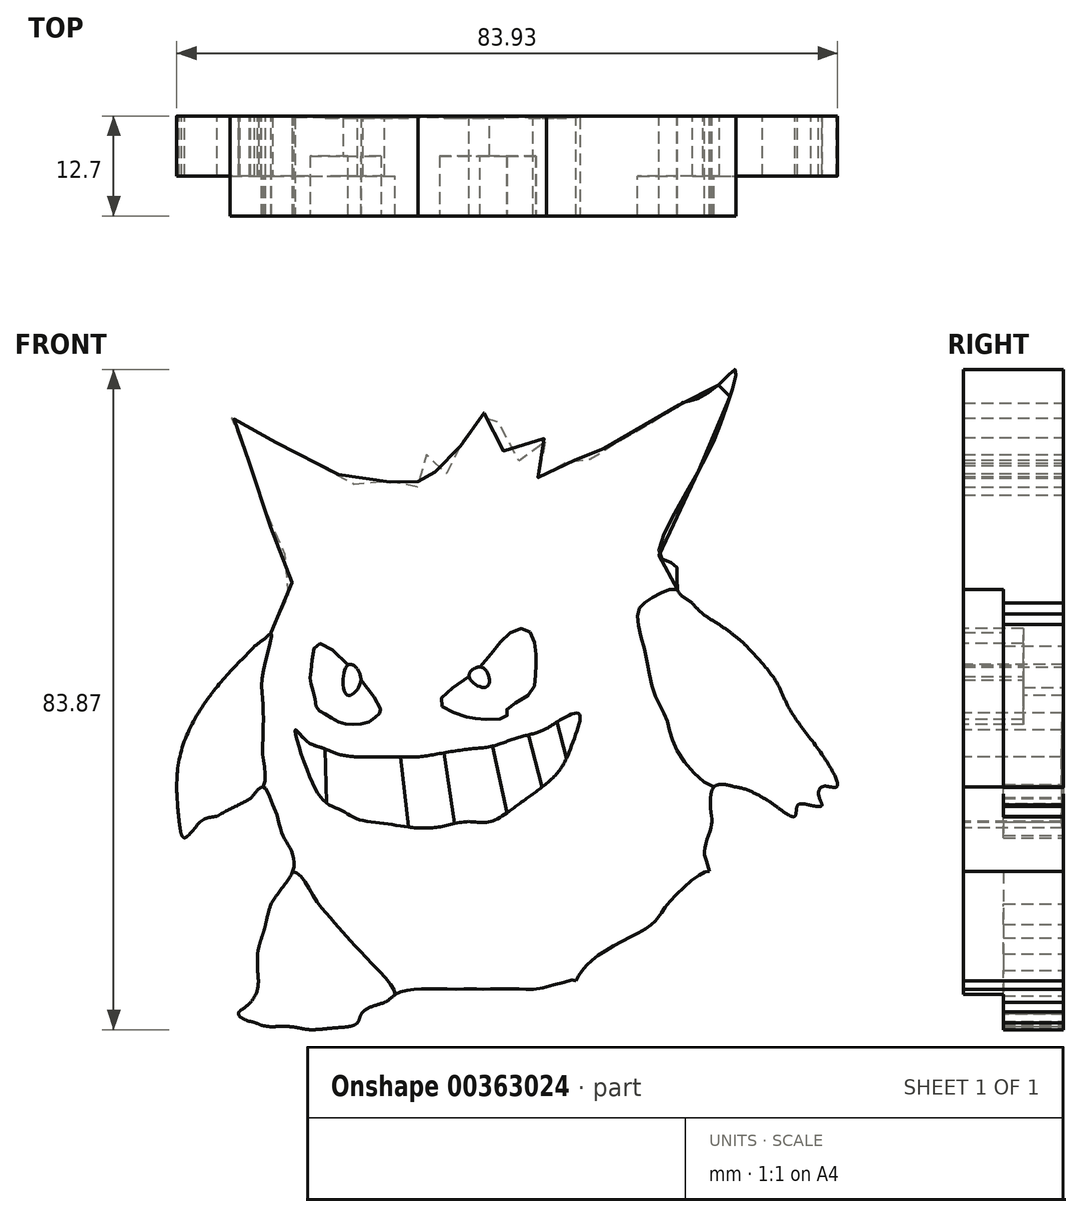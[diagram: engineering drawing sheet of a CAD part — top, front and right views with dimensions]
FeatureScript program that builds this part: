
annotation { "Feature Type Name" : "Feature", "Feature Type Description" : "" }
export const myFeature = defineFeature(function(context is Context, id is Id, definition is map)
    precondition{}
    {
        {
            var Q0;
            Q0=qCreatedBy(makeId("Front.planeOp"),FACE);
            var sketch = newSketch(context, id + "F0", { "sketchPlane" : qUnion([Q0])});
            skPoint(sketch, "E0.93.internal.snap0", {"position": v(-42.85, 9.92) * mm});
            skFitSpline(sketch, "E0", {"points": [v(-15.9, 37.28) * mm, v(-21.04, 39.5) * mm, v(-27.22, 42.6) * mm, v(-32.02, 45.34) * mm, v(-34.08, 46.36) * mm, v(-35.1, 46.88) * mm, v(-33.4, 42.93) * mm, v(-31.85, 38.48) * mm, v(-29.1, 31.1) * mm, v(-27.22, 27.16) * mm, v(-28.6, 22.35) * mm, v(-29.96, 19.61) * mm, v(-32.02, 17.9) * mm, v(-37.5, 11.9) * mm, v(-41.62, 3.49) * mm, v(-41.62, -4.4) * mm, v(-40.94, -6.46) * mm, v(-38.88, -4.4) * mm, v(-36.82, -3.71) * mm, v(-33.4, -2.34) * mm, v(-31, 0) * mm, v(-29.96, -1.66) * mm, v(-29.28, -3.37) * mm, v(-28.6, -5.77) * mm, v(-27.9, -7.14) * mm, v(-27.22, -8.52) * mm, v(-27.22, -10.75) * mm, v(-29.96, -14.86) * mm, v(-30.65, -17.43) * mm, v(-31.16, -19.15) * mm, v(-31.68, -21.2) * mm, v(-31.68, -23.27) * mm, v(-32.02, -25.15) * mm, v(-32.02, -25.67) * mm, v(-32.02, -26.52) * mm, v(-33.4, -28.07) * mm, v(-34.08, -28.75) * mm, v(-33.4, -29.95) * mm, v(-32.7, -29.78) * mm, v(-30.65, -30.47) * mm, v(-29.8, -30.47) * mm, v(-27.22, -30.47) * mm, v(-25.16, -30.81) * mm, v(-22.42, -30.64) * mm, v(-20.36, -30.47) * mm, v(-18.99, -29.95) * mm, v(-18.3, -28.58) * mm, v(-15.56, -27.38) * mm, v(-14.18, -26.35) * mm, v(-12.81, -25.84) * mm, v(-10.75, -25.67) * mm, v(-8, -25.67) * mm, v(-5.27, -25.67) * mm, v(-3.9, -25.67) * mm, v(-1.84, -25.67) * mm, v(1.6, -25.67) * mm, v(3.65, -25.67) * mm, v(7.77, -24.64) * mm, v(8.8, -24.64) * mm, v(8.8, -26.7) * mm, v(9.83, -27.9) * mm, v(10.86, -29.78) * mm, v(12.91, -30.81) * mm, v(13.26, -33.2) * mm, v(15.32, -31.5) * mm, v(18.06, -33.2) * mm, v(20.29, -33.2) * mm, v(20.8, -31.5) * mm, v(22.86, -31.5) * mm, v(24.92, -31.5) * mm, v(24.92, -29.78) * mm, v(23.55, -27.72) * mm, v(24.92, -22.92) * mm, v(24.92, -20.35) * mm, v(24.92, -17.78) * mm, v(24.92, -15.55) * mm, v(25.6, -13.66) * mm, v(25.6, -10.23) * mm, v(25.1, -8.17) * mm, v(25.95, -5.09) * mm, v(25.95, -3.37) * mm, v(26.3, 0) * mm, v(29.04, 0) * mm, v(32.47, -1.31) * mm, v(34.52, -2.69) * mm, v(36.58, -3.71) * mm, v(36.92, -2.34) * mm, v(38.64, -2.34) * mm, v(40.01, -2.34) * mm, v(39.67, -1.31) * mm, v(40.01, 0) * mm, v(41.87, 0) * mm, v(40.01, 4.17) * mm, v(35.9, 9.92) * mm, v(34.18, 13.44) * mm, v(31.1, 17.2) * mm, v(29.72, 18.58) * mm, v(26.98, 20.64) * mm, v(24.92, 22.01) * mm, v(23.55, 23.38) * mm, v(21.66, 25.1) * mm, v(21.49, 28.19) * mm, v(19.43, 29.21) * mm, v(23.9, 39.33) * mm, v(27.66, 47.57) * mm, v(29.04, 53.03) * mm, v(26.98, 51.17) * mm, v(23.55, 49.1) * mm, v(22.18, 48.77) * mm, v(20.8, 47.4) * mm, v(18.92, 46.36) * mm, v(16, 45.34) * mm, v(13.26, 43.28) * mm, v(11.37, 42.6) * mm, v(9.83, 40.88) * mm, v(8.63, 41.56) * mm, v(5.88, 40.02) * mm, v(4.68, 39.5) * mm, v(3.3, 39.5) * mm, v(5.02, 44.3) * mm, v(2.62, 42.25) * mm, v(0, 41.56) * mm, v(-1.66, 48.77) * mm, v(-3.2, 47.05) * mm, v(-4.24, 45.68) * mm, v(-5.78, 43.62) * mm, v(-6.64, 41.22) * mm, v(-8.7, 39.5) * mm, v(-10.07, 42.25) * mm, v(-11.27, 39.5) * mm, v(-11.44, 38.13) * mm, v(-13.84, 39.85) * mm, v(-15.9, 37.28) * mm]});
            skFitSpline(sketch, "E1", {"points": [v(-26.87, 7.26) * mm, v(-25.16, 1.6) * mm, v(-22.93, -2) * mm, v(-20.87, -3.03) * mm, v(-18.99, -4.06) * mm, v(-15.9, -4.57) * mm, v(-12.47, -5.09) * mm, v(-8.7, -5.09) * mm, v(-5.1, -4.4) * mm, v(-2.18, -4.4) * mm, v(1.77, -2) * mm, v(6.4, 1.77) * mm, v(8.45, 5.89) * mm, v(9.14, 9.32) * mm, v(6.4, 8.3) * mm, v(4.34, 7.1) * mm, v(1.25, 6.23) * mm, v(-1.84, 5.2) * mm, v(-4.4, 4.86) * mm, v(-8, 4.35) * mm, v(-11.27, 3.83) * mm, v(-13.5, 3.83) * mm, v(-17.27, 3.83) * mm, v(-18.99, 3.83) * mm, v(-21.39, 4.17) * mm, v(-23.1, 4.86) * mm, v(-25.5, 5.89) * mm, v(-26.87, 7.26) * mm]});
            skFitSpline(sketch, "E2", {"points": [v(-23.79, 18.24) * mm, v(-24.82, 15.15) * mm, v(-24.99, 13.44) * mm, v(-24.47, 11.72) * mm, v(-24.13, 10) * mm, v(-23.1, 9.32) * mm, v(-21.39, 8.3) * mm, v(-19.67, 7.95) * mm, v(-17.44, 8.3) * mm, v(-16.24, 9.32) * mm, v(-16.07, 10) * mm, v(-23.79, 18.24) * mm]});
            skFitSpline(sketch, "E3", {"points": [v(-8.52, 10.7) * mm, v(-5.27, 8.98) * mm, v(-3.2, 8.63) * mm, v(0, 8.98) * mm, v(0, 9.83) * mm, v(2.97, 11.9) * mm, v(3.65, 14.64) * mm, v(3.65, 17.2) * mm, v(2.62, 19.95) * mm, v(0, 19.27) * mm, v(-3.9, 14.8) * mm, v(-8.52, 10.7) * mm]});
            skFitSpline(sketch, "E4", {"points": [v(-20.17, 15.5) * mm, v(-20.36, 11.72) * mm, v(-18.55, 13.63) * mm, v(-20.17, 15.5) * mm]});
            skFitSpline(sketch, "E5", {"points": [v(-3.04, 15.15) * mm, v(-2.52, 12.75) * mm, v(-4.8, 14.08) * mm, v(-3.04, 15.15) * mm]});
            skFitSpline(sketch, "E6", {"points": [v(-29.96, 19.61) * mm, v(-31, 14.47) * mm, v(-31, 10.35) * mm, v(-31, 6.23) * mm, v(-31, 3.83) * mm, v(-31, 0) * mm, v(-36.82, -3.71) * mm, v(-40.94, -6.46) * mm, v(-41.62, -4.4) * mm, v(-41.62, 3.49) * mm, v(-37.5, 11.9) * mm, v(-32.02, 17.9) * mm, v(-29.96, 19.61) * mm]});
            skFitSpline(sketch, "E7", {"points": [v(26.3, 0) * mm, v(21.49, 4.86) * mm, v(20.29, 8.63) * mm, v(18.75, 11.9) * mm, v(17.37, 17.9) * mm, v(16.69, 22.35) * mm, v(18.75, 24.24) * mm, v(21.66, 25.1) * mm, v(23.55, 23.38) * mm, v(24.92, 22.01) * mm, v(26.98, 20.64) * mm, v(29.72, 18.58) * mm, v(31.1, 17.2) * mm, v(34.18, 13.44) * mm, v(35.9, 9.92) * mm, v(40.01, 4.17) * mm, v(41.87, 0) * mm, v(40.01, 0) * mm, v(40.01, -2.34) * mm, v(38.64, -2.34) * mm, v(36.92, -2.34) * mm, v(36.58, -3.71) * mm, v(34.52, -2.69) * mm, v(32.47, -1.31) * mm, v(29.04, 0) * mm, v(26.3, 0) * mm]});
            skFitSpline(sketch, "E8", {"points": [v(-27.22, -10.75) * mm, v(-24.47, -14) * mm, v(-21.39, -17.78) * mm, v(-18.3, -21.2) * mm, v(-14.18, -26.35) * mm, v(-15.56, -27.38) * mm, v(-18.3, -28.58) * mm, v(-18.99, -29.95) * mm, v(-20.36, -30.47) * mm, v(-22.42, -30.64) * mm, v(-25.16, -30.81) * mm, v(-27.22, -30.47) * mm, v(-29.8, -30.47) * mm, v(-32.7, -29.78) * mm, v(-34.08, -28.75) * mm, v(-32.02, -26.52) * mm, v(-31.68, -23.27) * mm, v(-31.68, -21.2) * mm, v(-31.16, -19.15) * mm, v(-30.65, -17.43) * mm, v(-29.96, -14.86) * mm, v(-27.22, -10.75) * mm]});
            skFitSpline(sketch, "E9", {"points": [v(8.8, -24.64) * mm, v(11.88, -21.2) * mm, v(18.4, -17.43) * mm, v(20.46, -14.86) * mm, v(25.7, -10.75) * mm, v(25.6, -13.66) * mm, v(24.92, -15.55) * mm, v(24.92, -17.78) * mm, v(24.92, -20.35) * mm, v(24.92, -22.92) * mm, v(23.55, -27.72) * mm, v(24.92, -29.78) * mm, v(24.92, -31.5) * mm, v(22.86, -31.5) * mm, v(20.8, -31.5) * mm, v(20.29, -33.2) * mm, v(18.06, -33.2) * mm, v(15.32, -31.5) * mm, v(13.26, -33.2) * mm, v(12.91, -30.81) * mm, v(10.86, -29.78) * mm, v(9.83, -27.9) * mm, v(8.8, -26.7) * mm, v(8.8, -24.64) * mm]});
            skLineSegment(sketch, "E10", {"start": v(-23.1, 4.86) * mm, "end": v(-22.93, -2) * mm});
            skLineSegment(sketch, "E11", {"start": v(-18.99, 3.83) * mm, "end": v(-17.27, -4.06) * mm});
            skLineSegment(sketch, "E12", {"start": v(-13.5, 3.83) * mm, "end": v(-12.47, -5.09) * mm});
            skLineSegment(sketch, "E13", {"start": v(-8, 4.35) * mm, "end": v(-6.65, -4.64) * mm});
            skLineSegment(sketch, "E14", {"start": v(-1.84, 5.2) * mm, "end": v(0, -3.3) * mm});
            skLineSegment(sketch, "E15", {"start": v(2.76, 6.63) * mm, "end": v(4.49, 0) * mm});
            skLineSegment(sketch, "E16", {"start": v(6.4, 8.3) * mm, "end": v(7.56, 3.64) * mm});
            skSolve(sketch);
        }
        {
            var Q0;
            Q0=makeQuery(id+"F0.imprint","IMPRINT",FACE,{"disambiguationData":[TD([[makeQuery(id+"F0.imprint","IMPRINT",EDGE,{"derivedFrom":sQuery(id+"F0.wireOp",EDGE,"E1")}),-1.0]])]});
            extrude(context, id + "F1", {"entities" : qUnion([Q0]), "depth" : 12.7 * mm});
        }
        {
            var Q0;
            {var subQ0=sQuery(id+"F0.wireOp",EDGE,"E7");var subQ1=sQuery(id+"F0.wireOp",EDGE,"E0");var subQ6=makeQuery(id+"F0.imprint","INTERSECT",VERTEX,{"disambiguationData":[OD(0.0)],"derivedFrom":[subQ1,subQ0]});Q0=makeQuery(id+"F0.imprint","IMPRINT",FACE,{"disambiguationData":[TD([[makeQuery(id+"F0.imprint","IMPRINT",EDGE,{"disambiguationData":[TD([[subQ6,-1.0]])],"derivedFrom":subQ1}),1.0]])]});}
            var Q1;
            {var subQ0=sQuery(id+"F0.wireOp",EDGE,"E6");var subQ1=sQuery(id+"F0.wireOp",EDGE,"E0");var subQ11=makeQuery(id+"F0.imprint","INTERSECT",VERTEX,{"disambiguationData":[OD(0.0)],"derivedFrom":[subQ1,subQ0]});Q1=makeQuery(id+"F0.imprint","IMPRINT",FACE,{"disambiguationData":[TD([[makeQuery(id+"F0.imprint","IMPRINT",EDGE,{"disambiguationData":[TD([[subQ11,1.0]])],"derivedFrom":subQ1}),1.0]])]});}
            var Q2;
            {var subQ0=sQuery(id+"F0.wireOp",EDGE,"E8");var subQ1=sQuery(id+"F0.wireOp",EDGE,"E0");var subQ16=makeQuery(id+"F0.imprint","INTERSECT",VERTEX,{"disambiguationData":[OD(2.0)],"derivedFrom":[subQ1,subQ0]});Q2=makeQuery(id+"F0.imprint","IMPRINT",FACE,{"disambiguationData":[TD([[makeQuery(id+"F0.imprint","IMPRINT",EDGE,{"disambiguationData":[TD([[subQ16,-1.0]])],"derivedFrom":subQ1}),1.0]])]});}
            var Q3;
            {var subQ0=sQuery(id+"F0.wireOp",EDGE,"E9");var subQ1=sQuery(id+"F0.wireOp",EDGE,"E0");var subQ4=makeQuery(id+"F0.imprint","INTERSECT",VERTEX,{"disambiguationData":[OD(0.0)],"derivedFrom":[subQ1,subQ0]});var subQ6=makeQuery(id+"F0.imprint","IMPRINT",VERTEX,{"derivedFrom":subQ0});Q3=makeQuery(id+"F0.imprint","IMPRINT",FACE,{"disambiguationData":[TD([[makeQuery(id+"F0.imprint","IMPRINT",EDGE,{"disambiguationData":[TD([[subQ6,-1.0],[subQ4,1.0]])],"derivedFrom":subQ0}),-1.0]])]});}
            extrude(context, id + "F2", {"entities" : qUnion([Q0, Q1, Q2, Q3]), "operationType" : NewBodyOperationType.ADD, "depth" : 7.62 * mm});
        }
        {
            var Q0;
            {var subQ0=sQuery(id+"F0.wireOp",EDGE,"E4");var subQ1=sQuery(id+"F0.wireOp",EDGE,"E2");var subQ2=makeQuery(id+"F0.imprint","INTERSECT",VERTEX,{"disambiguationData":[OD(0.0)],"derivedFrom":[subQ1,subQ0]});Q0=makeQuery(id+"F0.imprint","IMPRINT",FACE,{"disambiguationData":[TD([[makeQuery(id+"F0.imprint","IMPRINT",EDGE,{"disambiguationData":[TD([[subQ2,-1.0]])],"derivedFrom":subQ1}),1.0]])]});}
            var Q1;
            {var subQ0=sQuery(id+"F0.wireOp",EDGE,"E5");var subQ1=sQuery(id+"F0.wireOp",EDGE,"E3");var subQ2=makeQuery(id+"F0.imprint","INTERSECT",VERTEX,{"disambiguationData":[OD(0.0)],"derivedFrom":[subQ1,subQ0]});Q1=makeQuery(id+"F0.imprint","IMPRINT",FACE,{"disambiguationData":[TD([[makeQuery(id+"F0.imprint","IMPRINT",EDGE,{"disambiguationData":[TD([[subQ2,-1.0]])],"derivedFrom":subQ1}),1.0]])]});}
            extrude(context, id + "F3", {"entities" : qUnion([Q0, Q1]), "operationType" : NewBodyOperationType.ADD, "depth" : 5.08 * mm});
        }
        {
            var Q0;
            Q0=sQuery(id+"F0.wireOp",EDGE,"E4");
            extrude(context, id + "F4", {"bodyType" : ToolBodyType.SURFACE, "surfaceEntities" : qUnion([Q0]), "depth" : 5.08 * mm});
        }
        {
            var Q0;
            Q0=sQuery(id+"F0.wireOp",EDGE,"E4");
            var Q1;
            Q1=sQuery(id+"F0.wireOp",EDGE,"E5");
            extrude(context, id + "F5", {"bodyType" : ToolBodyType.SURFACE, "surfaceEntities" : qUnion([Q0, Q1]), "depth" : 12.7 * mm});
        }
        {
            var Q0;
            {var subQ0=sQuery(id+"F0.wireOp",EDGE,"E6");var subQ1=sQuery(id+"F0.wireOp",EDGE,"E0");Q0=makeQuery(id+"F2.opExtrude","SWEPT_EDGE",EDGE,{"disambiguationData":[OSD([subQ1,subQ0]),TDD([makeQuery(id+"F0.imprint","INTERSECT",VERTEX,{"disambiguationData":[OD(2.0)],"derivedFrom":[subQ1,subQ0]})])]});}
            fillet(context, id + "F6", {"entities" : qUnion([Q0]), "radius" : 5.08 * mm, "tangentPropagation" : true, "allowEdgeOverflow" : false});
        }
        {
            var Q0;
            {var subQ0=sQuery(id+"F0.wireOp",EDGE,"E10");Q0=makeQuery(id+"F0.imprint","IMPRINT",FACE,{"disambiguationData":[TD([[makeQuery(id+"F0.imprint","IMPRINT",EDGE,{"derivedFrom":subQ0}),-1.0]])]});}
            extrude(context, id + "F7", {"entities" : qUnion([Q0]), "operationType" : NewBodyOperationType.ADD, "depth" : 0.15 * mm});
        }
        {
            var Q0;
            {var subQ0=sQuery(id+"F0.wireOp",EDGE,"E10");Q0=makeQuery(id+"F0.imprint","IMPRINT",FACE,{"disambiguationData":[TD([[makeQuery(id+"F0.imprint","IMPRINT",EDGE,{"derivedFrom":subQ0}),1.0]])]});}
            var Q1;
            {var subQ0=sQuery(id+"F0.wireOp",EDGE,"E13");Q1=makeQuery(id+"F0.imprint","IMPRINT",FACE,{"disambiguationData":[TD([[makeQuery(id+"F0.imprint","IMPRINT",EDGE,{"derivedFrom":subQ0}),1.0]])]});}
            var Q2;
            {var subQ0=sQuery(id+"F0.wireOp",EDGE,"E15");Q2=makeQuery(id+"F0.imprint","IMPRINT",FACE,{"disambiguationData":[TD([[makeQuery(id+"F0.imprint","IMPRINT",EDGE,{"derivedFrom":subQ0}),1.0]])]});}
            extrude(context, id + "F8", {"entities" : qUnion([Q0, Q1, Q2]), "operationType" : NewBodyOperationType.ADD, "depth" : 0.25 * mm});
        }
        {
            var Q0;
            {var subQ0=sQuery(id+"F0.wireOp",EDGE,"E12");Q0=makeQuery(id+"F0.imprint","IMPRINT",FACE,{"disambiguationData":[TD([[makeQuery(id+"F0.imprint","IMPRINT",EDGE,{"derivedFrom":subQ0}),1.0]])]});}
            var Q1;
            {var subQ0=sQuery(id+"F0.wireOp",EDGE,"E14");Q1=makeQuery(id+"F0.imprint","IMPRINT",FACE,{"disambiguationData":[TD([[makeQuery(id+"F0.imprint","IMPRINT",EDGE,{"derivedFrom":subQ0}),1.0]])]});}
            var Q2;
            {var subQ0=sQuery(id+"F0.wireOp",EDGE,"E16");Q2=makeQuery(id+"F0.imprint","IMPRINT",FACE,{"disambiguationData":[TD([[makeQuery(id+"F0.imprint","IMPRINT",EDGE,{"derivedFrom":subQ0}),1.0]])]});}
            extrude(context, id + "F9", {"entities" : qUnion([Q0, Q1, Q2]), "operationType" : NewBodyOperationType.ADD, "depth" : 0.15 * mm});
        }
    });
